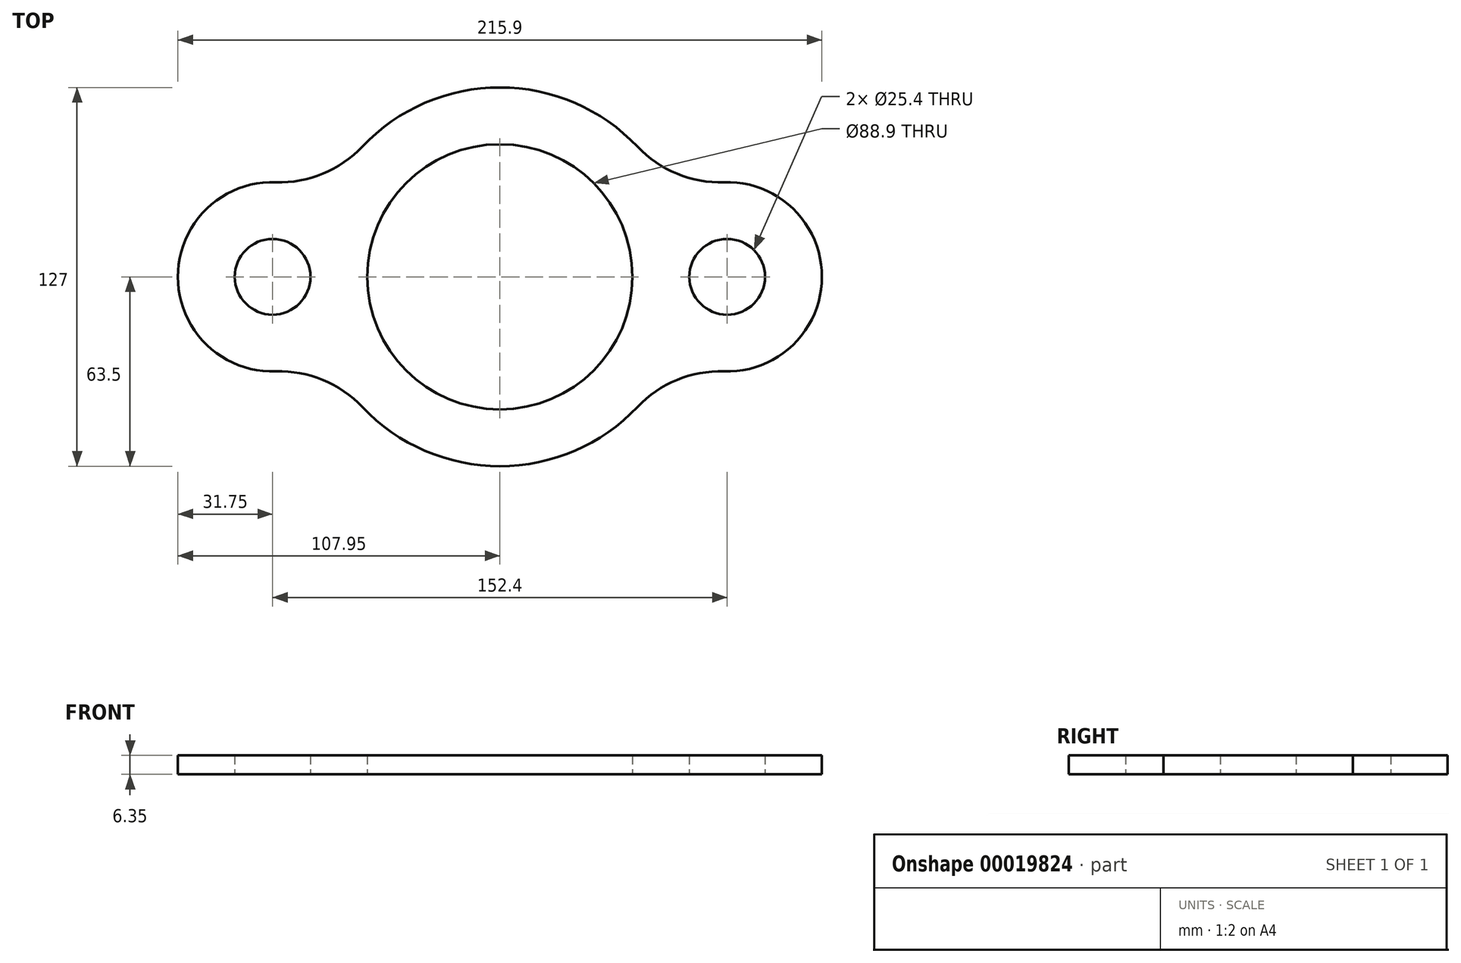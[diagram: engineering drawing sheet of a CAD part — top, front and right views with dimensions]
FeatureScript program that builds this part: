
annotation { "Feature Type Name" : "Feature", "Feature Type Description" : "" }
export const myFeature = defineFeature(function(context is Context, id is Id, definition is map)
    precondition{}
    {
        {
            var Q0;
            Q0=qCreatedBy(makeId("Top.planeOp"),FACE);
            var sketch = newSketch(context, id + "F0", { "sketchPlane" : qUnion([Q0])});
            skCircle(sketch, "E0", {"center": v(0, 0) * mm, "radius": 44.45 * mm});
            skArc(sketch, "E1", {"start": v(46.14, 43.63) * mm, "mid": v(0, 63.5) * mm, "end": v(-46.14, 43.63) * mm});
            skCircle(sketch, "E2", {"center": v(76.2, 0) * mm, "radius": 12.7 * mm});
            skCircle(sketch, "E3", {"center": v(-76.2, 0) * mm, "radius": 12.7 * mm});
            skArc(sketch, "E4", {"start": v(-75.12, 31.73) * mm, "mid": v(-107.95, 0) * mm, "end": v(-75.12, -31.73) * mm});
            skArc(sketch, "E5", {"start": v(75.12, -31.73) * mm, "mid": v(107.95, 0) * mm, "end": v(75.12, 31.73) * mm});
            skArc(sketch, "E6.trimOffspring", {"start": v(-46.14, -43.63) * mm, "mid": v(0, -63.5) * mm, "end": v(46.14, -43.63) * mm});
            skPoint(sketch, "E7.visualSharp", {"position": v(-57.94, 25.98) * mm});
            skArc(sketch, "E7.filletArc", {"start": v(-75.12, 31.73) * mm, "mid": v(-59.35, 34.56) * mm, "end": v(-46.14, 43.63) * mm});
            skPoint(sketch, "E8.visualSharp", {"position": v(57.94, 25.98) * mm});
            skArc(sketch, "E8.filletArc", {"start": v(46.14, 43.63) * mm, "mid": v(59.35, 34.56) * mm, "end": v(75.12, 31.73) * mm});
            skPoint(sketch, "E9.visualSharp", {"position": v(57.94, -25.98) * mm});
            skArc(sketch, "E9.filletArc", {"start": v(75.12, -31.73) * mm, "mid": v(59.35, -34.56) * mm, "end": v(46.14, -43.63) * mm});
            skPoint(sketch, "E10.visualSharp", {"position": v(-57.94, -25.98) * mm});
            skArc(sketch, "E10.filletArc", {"start": v(-46.14, -43.63) * mm, "mid": v(-59.35, -34.56) * mm, "end": v(-75.12, -31.73) * mm});
            skSolve(sketch);
        }
        {
            var Q0;
            Q0 = qSketchRegion(id + "F0", true);
            extrude(context, id + "F1", {"entities" : qUnion([Q0]), "depth" : 6.35 * mm});
        }
    });
